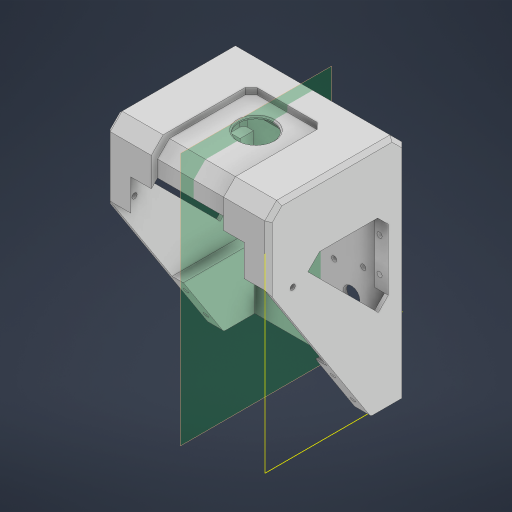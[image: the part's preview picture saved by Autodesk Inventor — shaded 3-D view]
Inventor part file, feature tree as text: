
AUTODESK INVENTOR PART (.ipt)
format: ipt  version: 2024 (Build 280153000, 153)  size: 708,096 bytes
history: native  units: in
note: dims shown in document units (in); Inventor stores cm internally (conversion verified against a paired STEP export)
features: sketch x26, extrude x25, projected_geometry x20, reference x12, other x10, plane x8, fillet x2, chamfer x2, mirror x2
ambient origin geometry x8: Origin, YZ Plane, XZ Plane, XY Plane, X Axis, Y Axis, Z Axis, Center Point
bodies: Solid1 (feature_tree)
feature tree (107):
  extrude  "Extrusion1"  Depth=5.1181in
  plane  "Work Plane1"
  plane  "Work Plane2"
  plane  "Work Plane3"
  plane  "Work Plane5"
  sketch  "Sketch3"  dims[d2=0.0689in d3=0.0689in]
  other  "Work Point1"
  other  "Work Point2"
  extrude  "Extrusion2"  Depth=0.0689in
  extrude  "Extrusion3"  [1 undecoded]
  extrude  "Extrusion4"  Depth=0.0157in
  extrude  "Extrusion5"  Depth=0.37in TaperAngle=0.0deg
  extrude  "Extrusion6"  Depth=0.2598in
  extrude  "Extrusion7"  Depth=0.2598in
  sketch  "Sketch9"  dims[d18=0.1378in d19=0.0in d21=0.37in d22=0.0in]
  plane  "Work Plane6"
  sketch  "Sketch10"  dims[d23=0.1181in d24=0.0787in]
  extrude  "Extrusion8"  Depth=0.37in TaperAngle=0.0deg
  extrude  "Extrusion9"  Depth=0.0787in
  extrude  "Extrusion10"  Depth=1.063in
  extrude  "Extrusion11"  Depth=1.4173in
  extrude  "Extrusion12"  Depth=3.1496in TaperAngle=0.0deg
  fillet  "Fillet2"  Radius=3.1496in
  sketch  "Sketch14"  dims[d38=0.1969in d40=0.1969in]
  extrude  "Extrusion13"  Depth=0.1969in
  plane  "Work Plane7"
  extrude  "Extrusion16"  TaperAngle=45.0deg  [1 undecoded]
  plane  "Work Plane9"
  sketch  "Sketch21"  dims[d48=0.0394in d49=0.1654in]
  plane  "Work Plane10"
  extrude  "Extrusion17"  Depth=0.1969in TaperAngle=0.0deg
  extrude  "Extrusion18"  Depth=0.0394in
  chamfer  "Chamfer3"  Distance=0.7676in
  extrude  "Extrusion19"  Depth=0.315in
  extrude  "Extrusion20"  Depth=0.315in
  mirror  "Mirror1"
  extrude  "Extrusion21"  Depth=0.1181in TaperAngle=45.0deg
  extrude  "Extrusion22"  TaperAngle=45.0deg  [1 undecoded]
  extrude  "Extrusion23"  Depth=0.1181in TaperAngle=0.0deg
  extrude  "Extrusion24"  Depth=1.9685in
  mirror  "Mirror2"
  extrude  "Extrusion25"  Depth=0.3543in TaperAngle=0.0deg
  fillet  "Fillet4"  Radius=0.1654in
  chamfer  "Chamfer4"  Distance=0.315in
  extrude  "Extrusion26"  Depth=0.3543in TaperAngle=0.0deg
  extrude  "Extrusion27"  Depth=0.1181in
  sketch  "Sketch1"  dims[d0=5.1181in d1=7.2in]
  reference  "Reference1"
  reference  "Reference2"
  reference  "Reference3"
  sketch  "Sketch4"  dims[d4=0.1181in d5=0.0in d6=-2.1654in]
  reference  "Reference4"
  sketch  "Sketch5"  dims[d7=-0.2165in d8=0.0157in]
  sketch  "Sketch6"  dims[d9=0.4606in d10=0.37in d11=0.0in]
  sketch  "Sketch7"  dims[d12=1.0in d13=0.0in d14=0.2598in]
  projected_geometry  "Projected Loop1"
  sketch  "Sketch8"  dims[d15=0.1378in d16=0.0in d17=0.2598in]
  projected_geometry  "Projected Loop2"
  projected_geometry  "Projected Loop3"
  reference  "Reference5"
  sketch  "Sketch11"  dims[d25=1.063in d26=0.0in d30=0.0197in]
  projected_geometry  "Projected Loop4"
  sketch  "Sketch12"  dims[d31=0.0787in d32=1.4173in]
  projected_geometry  "Projected Loop5"
  reference  "Reference6"
  sketch  "Sketch13"  dims[d33=0.0787in d34=3.1496in d35=0.0in d36=3.1496in d37=0.0in]
  projected_geometry  "Projected Loop6"
  reference  "Reference7"
  reference  "Reference8"
  projected_geometry  "Projected Loop7"
  sketch  "Sketch15"  dims[d41=0.0787in d42=0.0in d43=45.0deg]
  projected_geometry  "Projected Loop8"
  sketch  "Sketch19"  dims[d44=0.0787in d45=0.0in d46=0.1969in d47=0.0in]
  reference  "Reference9"
  projected_geometry  "Projected Loop15"
  reference  "Reference10"
  reference  "Reference11"
  reference  "Reference12"
  sketch  "Sketch22"  dims[d51=0.1654in]
  projected_geometry  "Projected Loop16"
  sketch  "Sketch23"  dims[d52=0.5906in]
  projected_geometry  "Projected Loop17"
  sketch  "Sketch25"  dims[d56=0.9843in]
  projected_geometry  "Projected Loop18"
  sketch  "Sketch26"  dims[d57=5.0in]
  projected_geometry  "Projected Loop19"
  sketch  "Sketch27"  dims[d58=8.8681in d59=0.309in d60=0.0in d61=0.0in]
  projected_geometry  "Projected Loop20"
  projected_geometry  "Projected Loop21"
  sketch  "Sketch28"  dims[d62=90.0deg]
  projected_geometry  "Projected Loop22"
  sketch  "Sketch29"  dims[d71=0.0079in d72=0.7676in d73=0.0in]
  projected_geometry  "Projected Loop23"
  sketch  "Sketch30"  dims[d74=0.7676in d75=0.0in d76=0.315in]
  projected_geometry  "Projected Loop24"
  sketch  "Sketch31"  dims[d77=0.315in d78=0.315in]
  projected_geometry  "Projected Loop25"
  sketch  "Sketch32"  dims[d79=0.1181in d80=0.0in d81=0.375in d82=0.125in d83=45.0deg d84=45.0deg d85=0.1181in d86=0.0in d87=1.9685in d88=0.3543in d89=0.0in d90=0.1654in d91=0.315in d92=0.3543in d93=0.0in d94=0.1654in d95=0.1654in d96=0.5906in d97=0.5906in d98=0.3543in d99=0.0in d101=45.0deg d102=0.3543in d103=0.0in d104=45.0deg d105=45.0deg d106=0.315in d107=1.0in d108=0.0in d109=0.1654in d110=0.1654in d111=0.4331in d112=0.4331in d113=0.1654in d114=1.0in d115=0.0in d116=0.1181in d117=0.1181in d118=0.125in d119=45.0deg d120=45.0deg d121=1.0in d122=0.0in d123=45.0deg d124=1.0in d125=0.0in]
  projected_geometry  "Projected Loop26"
  other  "<userpath>\Desktop\Camera_Mount.iam"
  other  "Camera_Mount.iam"
  other  "Head_Baseplate:1"
  other  "Camera_Baseplate:1"
  other  "<userpath>\Desktop\SeniorDesign\Head_V3\Head_V3_Assembly.iam"
  other  "Head_V3_Assembly.iam"
  other  "Emeet_Camera:1"
  other  "Camera_Clip:1"
note: 3 required parameter values undecoded (feature->parameter linkage not recoverable at this tier; creation-order binding heuristic only, values carry confidence <= 0.55)
